# Revit family: Rohrschelle Titan HD, halb Zoll, o.D
name_source: partatom
category: HLS-Bauteile
revit_build: Autodesk Revit 2017 (Build: 20190507_1515(x64)
units: mm (PartAtom-declared; Revit-internal decimal feet)

## family parameters
Arbeitsebenenbasiert = Ja
Beim Laden mit Abzugskörper schneiden = Nein
Bemaßung runder Anschluss = Durchmesser verwenden
Gemeinsam genutzt = Ja
Immer vertikal = Nein
Raumberechnungspunkt = Nein
Teiletyp = Normal

## types (21) — shared parameters
A = 20 mm  [stored 0.0656168 ft]
Anschluss = 1/2''
Anschlußhöhe = 20 mm
Bauart = zweiteilig
Brandschutz = RAL GZ 656
DF1 = 29 mm  [stored 0.0951444 ft]
DVS = 13 mm
Fabrikat = MEFA
Firma = MEFA Befestigungs- und Montagesysteme GmbH
HGA = 15 mm  [stored 0.0492126 ft]
Kurztext1 = Rohrschelle Titan HD 50x5,0
MB = 50 mm  [stored 0.164042 ft]
MD = 5 mm  [stored 0.0164042 ft]
Material = Stahl
Materialmaße = 50x5,0 mm
Materialname = S235
Mengeneinheit = St
Oberflaeche = galvanisch verzinkt
Verschluss = Schraubverschluss
Verschluss-Schraube = M12
Vorgabe-Ansicht = 1219 mm
max. zul. Last horizontal = 0.00 kN
max. zul. Last vertikal = 0.00 kN
vpe = 1 St
zero-valued in all types: Nennweite DN Rohr, Stärke Material, max. Rohraußendurchmesser, min. Rohraußendurchmesser

## per-type parameters (varying)
| type | Achsabstand | Artikelnummer | B | Breite | D | DF2 | EAN | Gewicht | Gewicht pro Bauteil | H | Höhe | Kurztext2 | R | RM | Rohraußendurchmesser | Rohraußendurchmesser Zoll | S | max. Höhe | max. zul. Last |
| Titan HD, 1/2", Ø 64, o.D. | 112 mm | 0072502 | 141 mm | 141 mm | 64 mm  [stored 0.209974 ft] | 13 mm | 4250928403827 | 0.78 kg | 0.78 kg | 89 mm  [stored 0.291995 ft] | 89 mm | 64 mm 1/2'' | 32 mm  [stored 0.104987 ft] | 37 mm  [stored 0.121391 ft] | 64 mm  [stored 0.209974 ft] | Zoll | 112 mm | 89 mm  [stored 0.291995 ft] | 6.00 kN |
| Titan HD, 1/2", Ø 76, o.D. | 124 mm | 0072507 | 154 mm | 153 mm | 76 mm  [stored 0.249344 ft] | 13 mm | 4250928403841 | 0.86 kg | 0.86 kg | 101 mm  [stored 0.331365 ft] | 101 mm | 76 mm 1/2'' | 38 mm  [stored 0.124672 ft] | 43 mm | 76 mm  [stored 0.249344 ft] | 2 1/2 Zoll | 125 mm | 101 mm  [stored 0.331365 ft] | 6.00 kN |
| Titan HD, 1/2", Ø 89, o.D. | 138 mm | 0072509 | 167 mm | 167 mm | 89 mm  [stored 0.291995 ft] | 13 mm | 4250928403865 | 0.94 kg | 0.94 kg | 114 mm | 114 mm | 89 mm 1/2'' | 45 mm  [stored 0.147638 ft] | 50 mm  [stored 0.164042 ft] | 89 mm  [stored 0.291995 ft] | 3 Zoll | 138 mm | 114 mm | 6.00 kN |
| Titan HD, 1/2", Ø108, o.D. | 157 mm | 0072514 | 186 mm | 186 mm | 108 mm  [stored 0.354331 ft] | 13 mm | 4250928403889 | 1.06 kg | 1.06 kg | 133 mm | 133 mm | 108 mm 1/2'' | 54 mm  [stored 0.177165 ft] | 59 mm  [stored 0.19357 ft] | 108 mm  [stored 0.354331 ft] | Zoll | 157 mm | 133 mm | 6.00 kN |
| Titan HD, 1/2", Ø110, o.D. | 159 mm | 0072517 | 188 mm | 188 mm | 110 mm  [stored 0.360892 ft] | 13 mm | 4250928403902 | 1.07 kg | 1.07 kg | 135 mm | 135 mm | 110 mm 1/2'' | 55 mm  [stored 0.180446 ft] | 60 mm  [stored 0.19685 ft] | 110 mm  [stored 0.360892 ft] | Zoll | 159 mm | 135 mm | 6.00 kN |
| Titan HD, 1/2", Ø114, o.D. | 163 mm | 0072519 | 192 mm | 192 mm | 114 mm | 13 mm | 4250928403919 | 1.10 kg | 1.10 kg | 139 mm | 139 mm | 114 mm 1/2'' | 57 mm  [stored 0.187008 ft] | 62 mm  [stored 0.203412 ft] | 114 mm | 4 Zoll | 163 mm | 139 mm | 6.00 kN |
| Titan HD, 1/2", Ø133, o.D. | 183 mm | 0072584 | 212 mm | 212 mm | 133 mm | 14 mm  [stored 0.0459318 ft] | 4250928403957 | 1.22 kg | 1.22 kg | 158 mm | 158 mm | 133 mm 1/2'' | 67 mm | 72 mm | 133 mm | Zoll | 183 mm | 158 mm | 6.00 kN |
| Titan HD, 1/2", Ø135, o.D. | 185 mm | 0072592 | 214 mm | 214 mm | 135 mm | 14 mm  [stored 0.0459318 ft] | 4250928403971 | 1.23 kg | 1.23 kg | 160 mm | 160 mm | 135 mm 1/2'' | 68 mm | 73 mm | 135 mm | Zoll | 185 mm | 160 mm | 6.00 kN |
| Titan HD, 1/2", Ø140, o.D. | 190 mm | 0072606 | 219 mm | 219 mm | 140 mm | 14 mm  [stored 0.0459318 ft] | 4250928403995 | 1.26 kg | 1.26 kg | 165 mm | 165 mm | 140 mm 1/2'' | 70 mm  [stored 0.229659 ft] | 75 mm  [stored 0.246063 ft] | 140 mm | 5 Zoll | 190 mm | 165 mm | 6.00 kN |
| Titan HD, 1/2", Ø160, o.D. | 210 mm | 0072649 | 239 mm | 239 mm | 160 mm | 14 mm  [stored 0.0459318 ft] | 4250928404039 | 1.39 kg | 1.39 kg | 185 mm | 185 mm | 160 mm 1/2'' | 80 mm  [stored 0.262467 ft] | 85 mm  [stored 0.278871 ft] | 160 mm | Zoll | 210 mm | 185 mm | 6.00 kN |
| Titan HD, 1/2", Ø165, o.D. | 215 mm | 0072681 | 244 mm | 244 mm | 165 mm | 14 mm  [stored 0.0459318 ft] | 4250928404053 | 1.42 kg | 1.42 kg | 190 mm | 190 mm | 165 mm 1/2'' | 83 mm | 88 mm | 165 mm | 6 Zoll | 215 mm | 190 mm | 6.00 kN |
| Titan HD, 1/2", Ø168, o.D. | 218 mm | 0072683 | 247 mm | 247 mm | 168 mm | 14 mm  [stored 0.0459318 ft] | 4250928404060 | 1.44 kg | 1.44 kg | 193 mm | 193 mm | 168 mm 1/2'' | 84 mm  [stored 0.275591 ft] | 89 mm  [stored 0.291995 ft] | 168 mm | Zoll | 218 mm | 193 mm | 6.00 kN |
| Titan HD, 1/2", Ø194, o.D. | 244 mm | 0072754 | 273 mm | 273 mm | 194 mm | 14 mm  [stored 0.0459318 ft] | 4250928404114 | 1.61 kg | 1.61 kg | 219 mm | 219 mm | 194 mm 1/2'' | 97 mm  [stored 0.318241 ft] | 102 mm  [stored 0.334646 ft] | 194 mm | Zoll | 244 mm | 219 mm | 16.00 kN |
| Titan HD, 1/2", Ø200, o.D. | 250 mm | 0072762 | 279 mm | 279 mm | 200 mm | 14 mm  [stored 0.0459318 ft] | 4250928404138 | 1.64 kg | 1.64 kg | 225 mm | 225 mm | 200 mm 1/2'' | 100 mm  [stored 0.328084 ft] | 105 mm  [stored 0.344488 ft] | 200 mm | Zoll | 250 mm | 225 mm | 16.00 kN |
| Titan HD, 1/2", Ø210, o.D. | 261 mm | 0072791 | 290 mm | 290 mm | 210 mm | 14 mm  [stored 0.0459318 ft] | 4250928404152 | 1.71 kg | 1.71 kg | 235 mm | 235 mm | 210 mm 1/2'' | 105 mm  [stored 0.344488 ft] | 110 mm  [stored 0.360892 ft] | 210 mm | Zoll | 261 mm | 235 mm | 16.00 kN |
| Titan HD, 1/2", Ø219, o.D. | 261 mm | 0072819 | 299 mm | 290 mm | 219 mm | 14 mm  [stored 0.0459318 ft] | 4250928404152 | 1.71 kg | 1.71 kg | 244 mm | 235 mm | 210 mm 1/2'' | 110 mm  [stored 0.360892 ft] | 115 mm | 210 mm | Zoll | 270 mm | 235 mm | 16.00 kN |
| Titan HD, 1/2", Ø267, o.D. | 318 mm | 0072892 | 347 mm | 347 mm | 267 mm | 14 mm  [stored 0.0459318 ft] | 4250928404213 | 2.07 kg | 2.07 kg | 292 mm | 292 mm | 267 mm 1/2'' | 134 mm | 139 mm | 267 mm | Zoll | 318 mm | 292 mm | 16.00 kN |
| Titan HD, 1/2", Ø273, o.D. | 324 mm | 0072894 | 353 mm | 353 mm | 273 mm | 14 mm  [stored 0.0459318 ft] | 4250928404237 | 2.11 kg | 2.11 kg | 298 mm | 298 mm | 273 mm 1/2'' | 137 mm | 142 mm | 273 mm | 10 Zoll | 324 mm | 298 mm | 16.00 kN |
| Titan HD, 1/2", Ø324, o.D. | 375 mm | 0072955 | 404 mm | 404 mm | 324 mm | 14 mm  [stored 0.0459318 ft] | 4250928404275 | 2.43 kg | 2.43 kg | 349 mm | 349 mm | 324 mm 1/2'' | 162 mm | 167 mm | 324 mm | 12 Zoll | 375 mm | 349 mm | 16.00 kN |
| Titan HD, 1/2", Ø356, o.D. | 407 mm | 0072965 | 436 mm | 436 mm | 356 mm | 14 mm  [stored 0.0459318 ft] | 4250928404299 | 2.64 kg | 2.64 kg | 381 mm | 381 mm | 356 mm 1/2'' | 178 mm | 183 mm | 356 mm | Zoll | 407 mm | 381 mm | 16.00 kN |
| Titan HD, 1/2", Ø368, o.D. | 419 mm | 0072967 | 448 mm | 448 mm | 368 mm | 14 mm  [stored 0.0459318 ft] | 4250928404312 | 2.71 kg | 2.71 kg | 393 mm | 393 mm | 368 mm 1/2'' | 184 mm | 189 mm | 368 mm | 14 Zoll | 419 mm | 393 mm | 16.00 kN |

note: [stored X ft] marks values corroborated as IEEE doubles in the binary element streams (Revit-internal decimal feet)

## geometry (parser evidence)
native form markers: Sweep x2
no freeform markers — native parametric forms only
